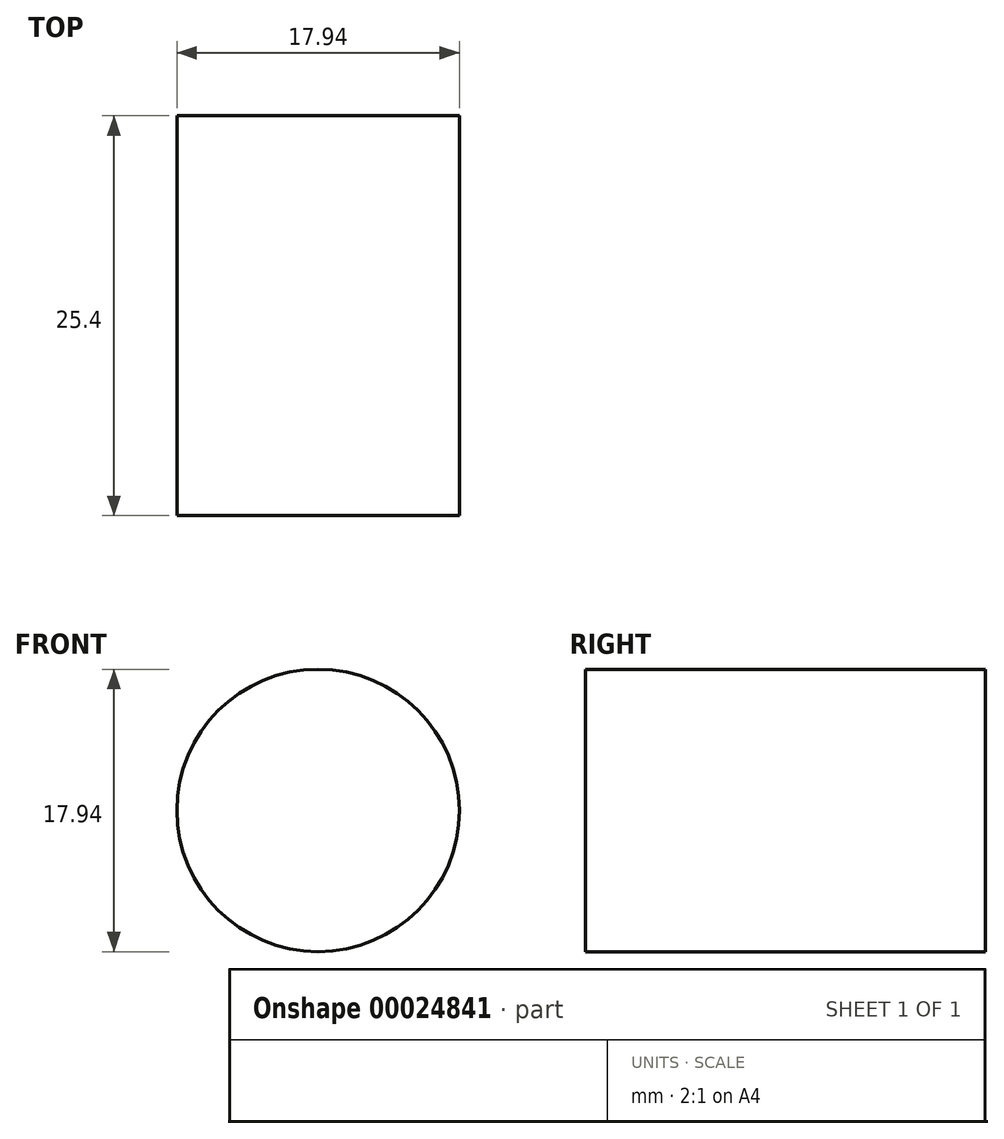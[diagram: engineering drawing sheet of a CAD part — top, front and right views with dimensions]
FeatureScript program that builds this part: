
annotation { "Feature Type Name" : "Feature", "Feature Type Description" : "" }
export const myFeature = defineFeature(function(context is Context, id is Id, definition is map)
    precondition{}
    {
        {
            var Q0;
            Q0=qCreatedBy(makeId("Front.planeOp"),FACE);
            var sketch = newSketch(context, id + "F0", { "sketchPlane" : qUnion([Q0])});
            skCircle(sketch, "E0", {"center": v(0, 0) * mm, "radius": 8.97 * mm});
            skSolve(sketch);
        }
        {
            var Q0;
            Q0=makeQuery(id+"F0.imprint","IMPRINT",FACE,{"disambiguationData":[TD([[makeQuery(id+"F0.imprint","IMPRINT",EDGE,{"derivedFrom":sQuery(id+"F0.wireOp",EDGE,"E0")}),1.0]])]});
            extrude(context, id + "F1", {"entities" : qUnion([Q0]), "depth" : 25.4 * mm});
        }
    });
